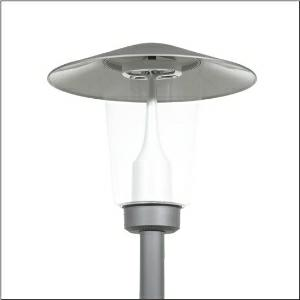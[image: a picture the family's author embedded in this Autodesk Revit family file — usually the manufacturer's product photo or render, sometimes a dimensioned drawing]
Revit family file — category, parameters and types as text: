
# Revit family: pilzleuchte_iq___st1_2a_5xa5235af14hp_844e
name_source: partatom
category: Lighting Fixtures
units: mm (PartAtom-declared; Revit-internal decimal feet)

## family parameters
Cut with Voids When Loaded = No
Host = Face
Light Source = No
Part Type = Normal
Room Calculation Point = No
Round Connector Dimension = Use Diameter
Shared = No

## types (1)
- --- (1 x LED, 3950 lm, 33.6 W, 2200K)
    Apparent Load = 34 VA
    CIE Flux Codes = 23 60 92 98 100
    Color Rendering = 70
    Color Temperature = 2200K
    Default Elevation = 1800 mm
    Description = Mushroom Luminaire iQ, mast luminaire, Module 540 iQ-SR, primary light control with 3 zone facetted reflector, of plastic, silver coated, highly specular, structured, primary optical cover: cover, of PMMA, transparent, light distribution: ST1.2a, light emission: direct distribution, primary light characteristic: asymmetric, installation type: post-top, LED, High Power LED, rated luminous flux: 3.950lm, luminous efficacy: 117lm/W, light colour: 722, colour temperature: 2200K, control gear: iQ Street-Remote, control: pre-setting: logarithmic dimming characteristic, Street-Remote, Auto-Match, Temp-Guard, Lumen-Switch, Night-Set, Smart-Wire, Light-Fading, Desk-Remote (wireless, voltage-free reading and setting of iQ features in the workshop via application-optimized NFC function/RFID function), optimised constant luminous flux control (CLO 2.0), with terminal, 6-pole, max. 2.5mm², mains connection: 230..240V, AC, 50/60Hz, start of lifetime: 34W, end of service life: 36W, reduction: 15W, luminaire housing, upper part, of glass-fibre reinforced polyester, coated, Siteco® metallic grey (DB 702S), diameter: 650mm, height: 586mm, spigot size: d x l = 76 x 70mm (post-top) | with reducer (optional accessory) 60 x 70mm, mounting height: 3..5m, post-top mast mounting element, of diecast aluminium, coated, Siteco® metallic grey (DB 702S), Module 540 iQ-SR, traffic white (RAL 9016), equipment: Power, protection rating (complete): IP65, insulation class (complete): insulation class II (safety insulation), certification: CE, ENEC, VDE, packaging unit: 1 piece

Light Distribution: ST1.2a
    Height = 586 mm
    Lamp = 1 x LED
    Lamp Light Flux = 3950 lm
    Lamp Power = 33.6 W
    Lamp count = 1
    Length = 650 mm
    Luminous efficacy = 118 lm/W
    Manufacturer = Siteco
    ModVariant = No
    Model = 5XA5235AF14HP
    Number of Poles = 1
    OnlyDefault = Yes
    Power Factor = 1
    Product Name = Pilzleuchte iQ | ST1.2a
    Product group = mast luminaire | pylon top
    ProductGroupID = 6100
    Protection Class = Protection class II
    Protection Degree = IP 65
    RLX_Detail_Level = 1
    RLX_Emergency_Light_Flux = 0 lm
    RLX_Emergency_Type = 0
    RLX_Emergency_Type_DB = No
    RlxData = <blob elided: 51621 chars, md5=a511a10d>
    Socket = socket
    Standby Power = 0 W
    System Light Flux = 3950 lm
    System Power = 34 W
    Type Comments = factory setting: luminous flux: 100 % | dim-lin: 254 | 695 mA
    Type Image = l_1006077.jpg
    URL = http://relux.com
    VarID = @adj_191123
    Voltage = 0 V
    Weight = 0.00 kg
    Width = 0 mm  [stored 0 ft]

note: [stored X ft] marks values corroborated as IEEE doubles in the binary element streams (Revit-internal decimal feet)

## geometry (parser evidence)
native form markers: Blend x4, Sweep x9
no freeform markers — native parametric forms only
